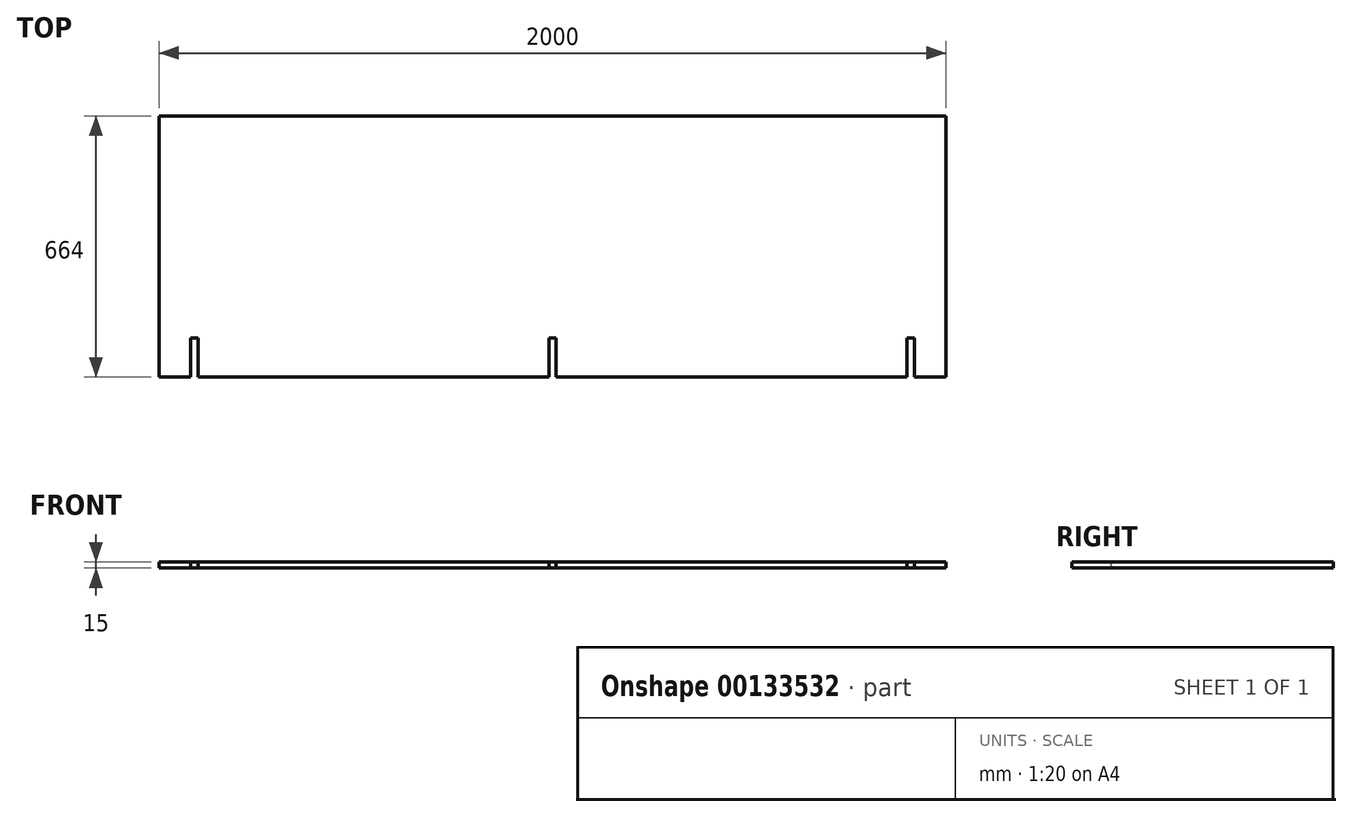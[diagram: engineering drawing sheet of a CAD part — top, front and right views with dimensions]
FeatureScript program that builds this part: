
annotation { "Feature Type Name" : "Feature", "Feature Type Description" : "" }
export const myFeature = defineFeature(function(context is Context, id is Id, definition is map)
    precondition{}
    {
        {
            var Q0;
            Q0=qCreatedBy(makeId("Right.planeOp"),FACE);
            var sketch = newSketch(context, id + "F0", { "sketchPlane" : qUnion([Q0])});
            skLineSegment(sketch, "E0.bottom", {"start": v(332, -7.5) * mm, "end": v(-332, -7.5) * mm});
            skLineSegment(sketch, "E0.top", {"start": v(332, 7.5) * mm, "end": v(-332, 7.5) * mm});
            skLineSegment(sketch, "E0.left", {"start": v(332, -7.5) * mm, "end": v(332, 7.5) * mm});
            skLineSegment(sketch, "E0.right", {"start": v(-332, -7.5) * mm, "end": v(-332, 7.5) * mm});
            skPoint(sketch, "E0.middle", {"position": v(0, 0) * mm});
            skSolve(sketch);
        }
        {
            var Q0;
            Q0=makeQuery(id+"F0.imprint","IMPRINT",FACE,{"disambiguationData":[TD([[makeQuery(id+"F0.imprint","IMPRINT",EDGE,{"derivedFrom":sQuery(id+"F0.wireOp",EDGE,"E0.bottom")}),-1.0]])]});
            extrude(context, id + "F1", {"entities" : qUnion([Q0]), "endBound" : BoundingType.SYMMETRIC, "depth" : 2000 * mm});
        }
        {
            var Q0;
            Q0=makeQuery(id+"F1.opExtrude","SWEPT_FACE",FACE,{"disambiguationData":[OSD([sQuery(id+"F0.wireOp",EDGE,"E0.top")])]});
            var sketch = newSketch(context, id + "F2", { "sketchPlane" : qUnion([Q0])});
            skLineSegment(sketch, "E1", {"start": v(-1000, -332) * mm, "end": v(-919, -332) * mm});
            skLineSegment(sketch, "E2", {"start": v(-919, -332) * mm, "end": v(-919, -232) * mm});
            skLineSegment(sketch, "E3", {"start": v(-919, -232) * mm, "end": v(-900, -232) * mm});
            skLineSegment(sketch, "E4", {"start": v(-900, -232) * mm, "end": v(-900, -332) * mm});
            skLineSegment(sketch, "E5", {"start": v(-900, -332) * mm, "end": v(900, -332) * mm});
            skLineSegment(sketch, "E6", {"start": v(900, -332) * mm, "end": v(900, -232) * mm});
            skLineSegment(sketch, "E7", {"start": v(900, -232) * mm, "end": v(919, -232) * mm});
            skLineSegment(sketch, "E8", {"start": v(919, -232) * mm, "end": v(919, -332) * mm});
            skLineSegment(sketch, "E9", {"start": v(919, -332) * mm, "end": v(1000, -332) * mm});
            skLineSegment(sketch, "E10", {"start": v(0, -232) * mm, "end": v(-9.5, -232) * mm});
            skPoint(sketch, "E10.startSnap0", {"position": v(0, -332) * mm});
            skLineSegment(sketch, "E11", {"start": v(0, -232) * mm, "end": v(9.5, -232) * mm});
            skLineSegment(sketch, "E12", {"start": v(9.5, -232) * mm, "end": v(9.5, -332) * mm});
            skLineSegment(sketch, "E13", {"start": v(-9.5, -232) * mm, "end": v(-9.5, -332) * mm});
            skSolve(sketch);
        }
        {
            var Q0;
            {var subQ6=sQuery(id+"F2.wireOp",EDGE,"E1");Q0=makeQuery(id+"F2.imprint","IMPRINT",FACE,{"disambiguationData":[TD([[makeQuery(id+"F2.imprint","IMPRINT",EDGE,{"derivedFrom":subQ6}),1.0]])]});}
            var Q1;
            {var subQ0=sQuery(id+"F2.wireOp",EDGE,"E2");Q1=makeQuery(id+"F2.imprint","IMPRINT",FACE,{"disambiguationData":[TD([[makeQuery(id+"F2.imprint","IMPRINT",EDGE,{"derivedFrom":subQ0}),-1.0]])]});}
            var Q2;
            {var subQ0=sQuery(id+"F2.wireOp",EDGE,"E6");Q2=makeQuery(id+"F2.imprint","IMPRINT",FACE,{"disambiguationData":[TD([[makeQuery(id+"F2.imprint","IMPRINT",EDGE,{"derivedFrom":subQ0}),-1.0]])]});}
            var Q3;
            Q3=makeQuery(id+"F2.imprint","IMPRINT",FACE,{"disambiguationData":[TD([[makeQuery(id+"F2.imprint","IMPRINT",EDGE,{"derivedFrom":sQuery(id+"F2.wireOp",EDGE,"E10")}),1.0]])]});
            extrude(context, id + "F3", {"entities" : qUnion([Q0, Q1, Q2, Q3]), "operationType" : NewBodyOperationType.REMOVE, "oppositeDirection" : true, "depth" : 25 * mm});
        }
    });
